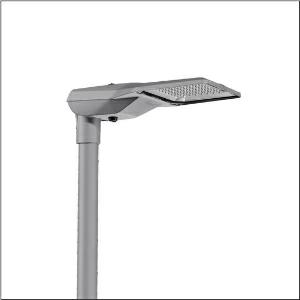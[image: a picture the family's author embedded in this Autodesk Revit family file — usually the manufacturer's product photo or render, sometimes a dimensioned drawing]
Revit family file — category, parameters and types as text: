
# Revit family: streetlight_sl_21_iq_midi___st1_0a_5xe3d31y08nb_4ee3
name_source: partatom
category: Lighting Fixtures
units: mm (PartAtom-declared; Revit-internal decimal feet)

## family parameters
Cut with Voids When Loaded = No
Host = Face
Light Source = No
Part Type = Normal
Room Calculation Point = No
Round Connector Dimension = Use Diameter
Shared = No

## types (1)
- --- (1 x LED, 21550 lm, 136.6 W, 3000K)
    Apparent Load = 137 VA
    CIE Flux Codes = 40 73 97 100 100
    Color Rendering = 70
    Color Temperature = 3000K
    Default Elevation = 1800 mm
    Description = Streetlight SL 21 iQ midi, mast luminaire, primary light control with lens, of PMMA, primary optical cover: cover, of toughened safety glass, transparent, light distribution: ST1.0a, light emission: direct distribution, primary light characteristic: asymmetric, installation type: post-top, side-entry, LED, High Power LED, rated luminous flux: 21.550lm, luminous efficacy: 158lm/W, light colour: 730, colour temperature: 3000K, control: presetting dimming logarithmic, Street-Remote, Auto-Match, Temp-Guard, Lumen-Switch, Night-Set, Smart-Wire, Light-Fading, Desk-Remote (wireless, voltage-free reading and setting of iQ features in the workshop via application-optimized NFC function/RFID function), optimised constant luminous flux control (CLO 2.0), mains connection: 230..240V, AC, 50/60Hz, start of lifetime: 137W, end of service life: 144W, reduction: 61W, luminaire housing, of diecast aluminium, powder-coated, Siteco® metallic grey (DB 702S), corrosivity category C5 mid according to DIN EN ISO 12944, please order mast flange separately, inclination adjustable: 0°, 5°, 10°, 15°, sealing non-destructively replaceable, multi-level sealing system, length: 644mm, width: 335mm, height: 110mm, mast flange for spigot size: 42mm (side-entry): 5XC10008XM4, 60/48mm (side-entry/post-top): 5XC10108XM2, 76/60mm (side-entry/post-top): 5XC10108XM1, Smart Interface below and above, protection rating (complete): IP66, insulation class (complete): insulation class II (safety insulation), certification: CE, ENEC, ENEC+, VDE, impact resistance: IK09, permissible operating ambient temperature for outdoor applications: -40..+50°C, standard-compliant lighting for roads and squares, packaging unit: 1 piece

Light Distribution: ST1.0a
    Height = 111 mm
    Lamp = 1 x LED
    Lamp Light Flux = 21550 lm
    Lamp Power = 136.6 W
    Lamp count = 1
    Length = 644 mm
    Luminous efficacy = 158 lm/W
    Manufacturer = Siteco
    ModVariant = No
    Model = 5XE3D31Y08NB
    Number of Poles = 1
    OnlyDefault = Yes
    Power Factor = 1
    Product Name = Streetlight SL 21 iQ midi | ST1.0a
    Product group = mast luminaire | pylon top
    ProductGroupID = 6100
    Protection Class = Protection class II
    Protection Degree = IP 66
    RLX_Detail_Level = 1
    RLX_Emergency_Light_Flux = 0 lm
    RLX_Emergency_Type = 0
    RLX_Emergency_Type_DB = No
    RlxData = <blob elided: 90781 chars, md5=5f5c626c>
    Socket = socket
    Standby Power = 0 W
    System Light Flux = 21550 lm
    System Power = 137 W
    Type Comments = factory setting: luminous flux: 100 % | dim-lin: 254 | 733 mA
    Type Image = l_1004304.jpg
    URL = http://relux.com
    VarID = @adj_043845
    Voltage = 0 V
    Weight = 0.00 kg
    Width = 336 mm

## geometry (parser evidence)
native form markers: Blend x4, Sweep x10
no freeform markers — native parametric forms only
